# Revit family: Vitra-Built-inBath&ShowerMixer(Exposedpart)-OriginSeries-A42621
name_source: partatom
category: Plumbing Fixtures
revit_build: Autodesk Revit 2017 (Build: 20160225_1515(x64)
units: mm (PartAtom-declared; Revit-internal decimal feet)

## family parameters
Cut with Voids When Loaded = No
Host = Face
OmniClass Number = 23.45.55.17
OmniClass Title = Mixing Faucets
Part Type = Normal
Room Calculation Point = No
Round Connector Dimension = Use Diameter
Shared = Yes

## types (4) — shared parameters
BIMobject category = Bath/Shower Mixer
CW Connection = Yes
Connection Diameter (mm) = 10 mm  [stored 0.0328084 ft]
Default Elevation = 850 mm  [stored 2.78871 ft]
Description = To clean your product use a soft cloth soaked in alcohol or soap. Never use. acid or hydrochloric acid used to clean closed and floor and never use cleaning salt used to clean basin and sink.
Design country = Turkey
HW Connection = Yes
Hot Water Supply (max.) = 80 °C
Hot Water temperature, factory set to = 38 °C
IFC Classification = Sanitary Terminal
Main Material = Brass
Manufacturer = Vitra
Manufacturer name = Vitra
Masterformat 2014 Code = 22 40 00
Masterformat 2014 Description = Plumbing Fixtures
Min. flow pressure of = 0.5 bar
MountingType = Wall-mounted (exposed part)
NBS Referans Code = 45-35-70/315
NBS Referans Description = Water supply fittings for baths
Nominal height = 0.000
Nominal width = 0.000
Number Of Connections = 2 mm  [stored 0.00656168 ft]
OmniClass Code = 23.45.55.17
OmniClass Description = Mixing Faucets
Product Properties = Energy Saving
Product Type = Built-in bath/shower mixer (exposed part)
Product certification = https://vitraglobal.com
Product data url = https://www.vitra.com.tr
Product family = Origin
Product group = Bath&Shower Mixer (exposed part)
Range of Hot Water Supply = 5 - 65 °C
Range of flow pressure = 1 - 5 bar
Technical description = https://www.vitra.com.tr
Test Pressure = 16 bar
UNSPSC Code = 301815
URL = https://vitraglobal.com
Uniclass 1.4 Code = L725111
Uniclass 1.4 Description = Mixer taps
Uniclass 2.0 Code = Pr_40_20_87_09
Uniclass 2.0 Description = Bath taps
Uniclass 2015 Code = Pr_40_20_87_09
Uniclass 2015 Name = Bath taps
Uniformat II Code = 22 40 00
Uniformat II Description = Plumbing Fixture
Warranty Period (Year) = 10 Years
Weight Net (kg) = 0.715
Youtube = https://www.youtube.com
zero-valued in all types: CWFU, Cost, HWFU, WFU

## per-type parameters (varying)
| type | Article No. (default) | Coating Material | Color | Depth(mm) | Height(mm) | Model | Product SKU | Width(mm) |
| Bath&ShowerMixer(Built-in)-Vitra-OriginSeries(Chrome)-A42621 | A42621 | Vitra-Chrome | Chrome | 138 mm | 84 mm | A42621 | A42621 | 120 mm |
| Bath&ShowerMixer(Built-in)-Vitra-OriginSeries(BrightCopper)-A4262126 | A4262126 | Vitra-BrightCopper | Bright Copper | 195 mm | 109 mm | A4262126 | A4262126 | 170 mm  [stored 0.557743 ft] |
| Bath&ShowerMixer(Built-in)-Vitra-OriginSeries(Nickel)-A4262134 | A4262134 | Vitra-Nickel | Nickel | 195 mm | 109 mm | A4262134 | A4262134 | 170 mm  [stored 0.557743 ft] |
| Bath&ShowerMixer(Built-in)-Vitra-OriginSeries(MatteBlack)-A4262136 | A4262136 | Vitra-MatteBlack | Matte Black | 195 mm | 109 mm | A4262136 | A4262136 | 170 mm  [stored 0.557743 ft] |

note: [stored X ft] marks values corroborated as IEEE doubles in the binary element streams (Revit-internal decimal feet)

## geometry (parser evidence)
native form markers: Sweep x3
no freeform markers — native parametric forms only
